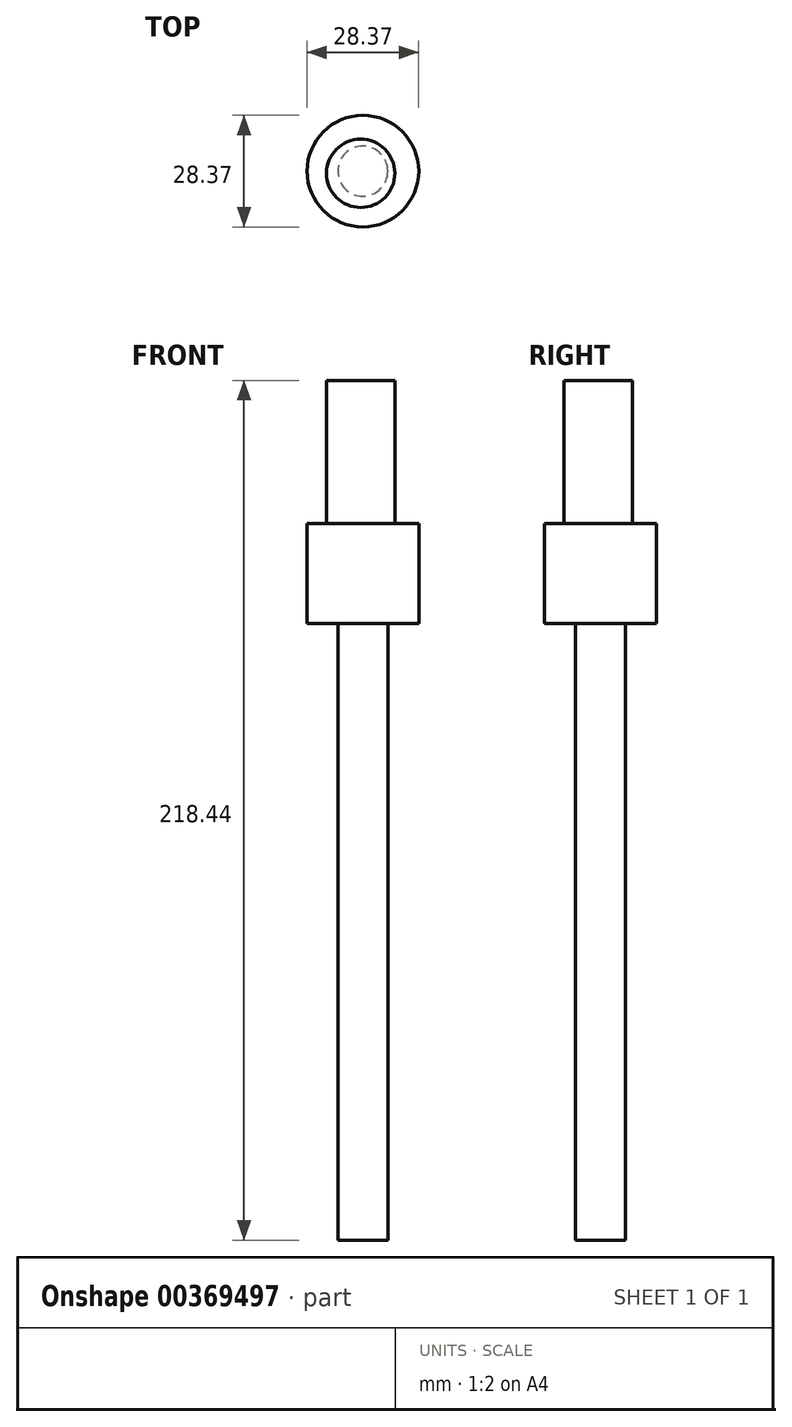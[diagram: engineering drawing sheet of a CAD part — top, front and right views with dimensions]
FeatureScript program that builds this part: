
annotation { "Feature Type Name" : "Feature", "Feature Type Description" : "" }
export const myFeature = defineFeature(function(context is Context, id is Id, definition is map)
    precondition{}
    {
        {
            var Q0;
            Q0=qCreatedBy(makeId("Top.planeOp"),FACE);
            var sketch = newSketch(context, id + "F0", { "sketchPlane" : qUnion([Q0])});
            skCircle(sketch, "E0", {"center": v(-31.22, 36.7) * mm, "radius": 8.68 * mm});
            skSolve(sketch);
        }
        {
            var Q0;
            Q0=makeQuery(id+"F0.imprint","IMPRINT",FACE,{"disambiguationData":[TD([[makeQuery(id+"F0.imprint","IMPRINT",EDGE,{"derivedFrom":sQuery(id+"F0.wireOp",EDGE,"E0")}),1.0]])]});
            extrude(context, id + "F1", {"entities" : qUnion([Q0]), "depth" : 61.72 * mm});
        }
        {
            var Q0;
            Q0=qCreatedBy(makeId("Top.planeOp"),FACE);
            var sketch = newSketch(context, id + "F2", { "sketchPlane" : qUnion([Q0])});
            skCircle(sketch, "E1", {"center": v(-30.65, 37.26) * mm, "radius": 14.19 * mm});
            skSolve(sketch);
        }
        {
            var Q0;
            Q0 = qSketchRegion(id + "F2", true);
            extrude(context, id + "F3", {"entities" : qUnion([Q0]), "operationType" : NewBodyOperationType.ADD, "depth" : 25.4 * mm});
        }
        {
            var Q0;
            Q0=makeQuery(id+"F3.boolean.opBoolean","MERGE",FACE,{"derivedFrom":[makeQuery(id+"F1.opExtrude","CAP_FACE",FACE,{"disambiguationData":[OSD([sQuery(id+"F0.wireOp",EDGE,"E0")])],"isStart":true}),makeQuery(id+"F3.opExtrude","CAP_FACE",FACE,{"disambiguationData":[OSD([sQuery(id+"F2.wireOp",EDGE,"E1")])],"isStart":true})]});
            var sketch = newSketch(context, id + "F4", { "sketchPlane" : qUnion([Q0])});
            skCircle(sketch, "E2", {"center": v(-30.65, -37.26) * mm, "radius": 6.35 * mm});
            skSolve(sketch);
        }
        {
            var Q0;
            Q0=makeQuery(id+"F4.imprint","IMPRINT",FACE,{"disambiguationData":[TD([[makeQuery(id+"F4.imprint","IMPRINT",EDGE,{"derivedFrom":sQuery(id+"F4.wireOp",EDGE,"E2")}),1.0]])]});
            extrude(context, id + "F5", {"entities" : qUnion([Q0]), "operationType" : NewBodyOperationType.ADD, "depth" : 156.72 * mm});
        }
    });
